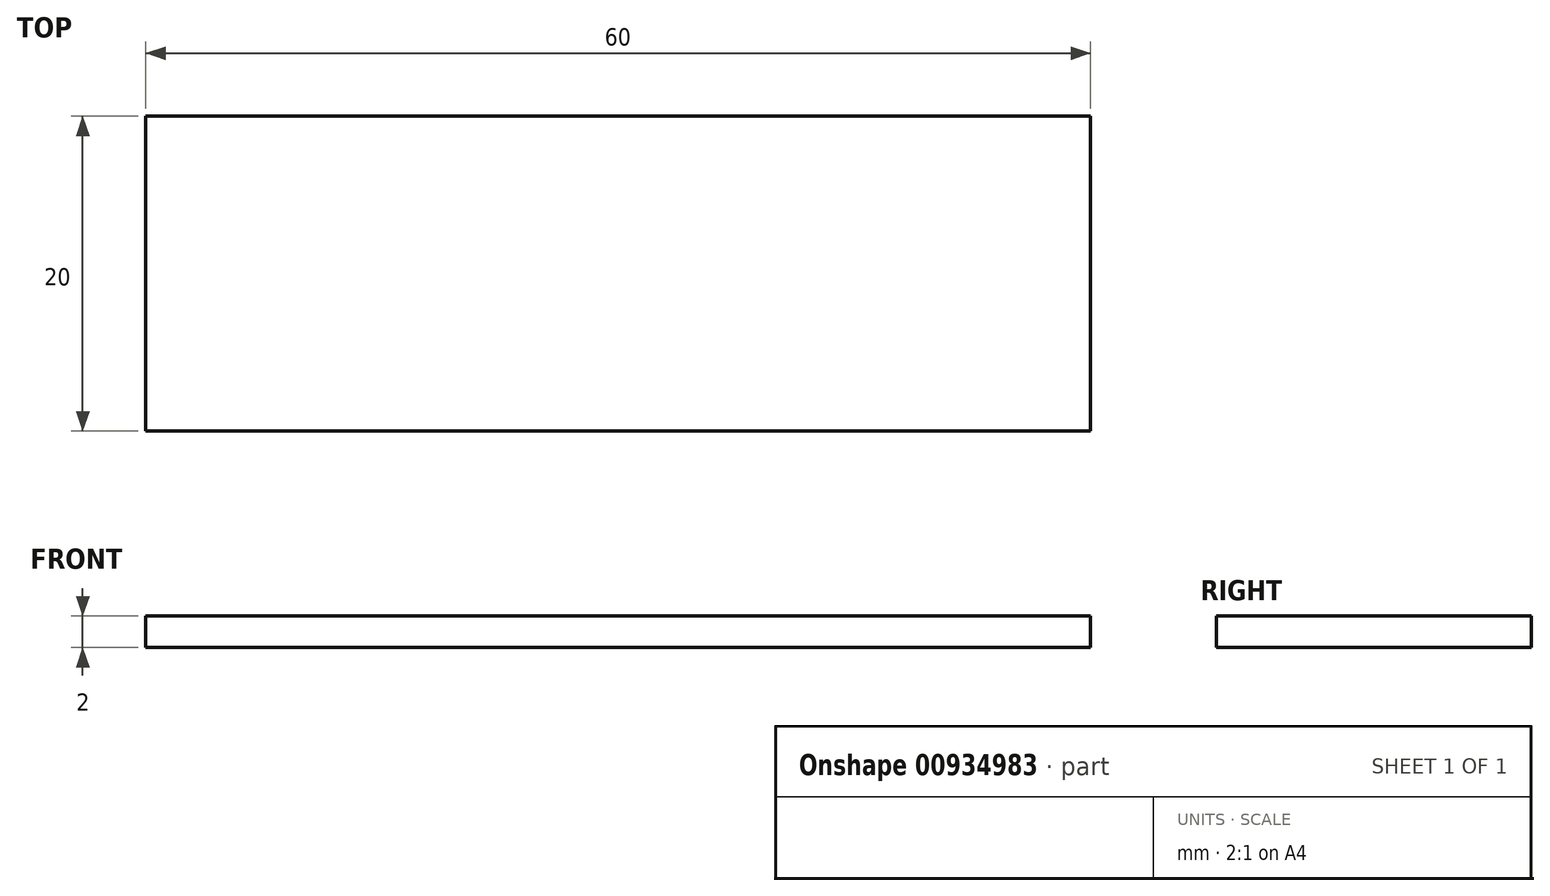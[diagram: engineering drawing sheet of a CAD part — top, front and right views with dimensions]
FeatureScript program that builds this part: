
annotation { "Feature Type Name" : "Feature", "Feature Type Description" : "" }
export const myFeature = defineFeature(function(context is Context, id is Id, definition is map)
    precondition{}
    {
        {
            var Q0;
            Q0=qCreatedBy(makeId("Top.planeOp"),FACE);
            var sketch = newSketch(context, id + "F0", { "sketchPlane" : qUnion([Q0])});
            skLineSegment(sketch, "E0.bottom", {"start": v(30, -10) * mm, "end": v(-30, -10) * mm});
            skLineSegment(sketch, "E0.top", {"start": v(30, 10) * mm, "end": v(-30, 10) * mm});
            skLineSegment(sketch, "E0.left", {"start": v(30, -10) * mm, "end": v(30, 10) * mm});
            skLineSegment(sketch, "E0.right", {"start": v(-30, -10) * mm, "end": v(-30, 10) * mm});
            skPoint(sketch, "E0.middle", {"position": v(0, 0) * mm});
            skLineSegment(sketch, "E1.bottom", {"start": v(-73.3, -58.13) * mm, "end": v(-88.16, -58.13) * mm});
            skLineSegment(sketch, "E1.top", {"start": v(-73.3, -35.95) * mm, "end": v(-88.16, -35.95) * mm});
            skLineSegment(sketch, "E1.left", {"start": v(-73.3, -58.13) * mm, "end": v(-73.3, -35.95) * mm});
            skLineSegment(sketch, "E1.right", {"start": v(-88.16, -58.13) * mm, "end": v(-88.16, -35.95) * mm});
            skPoint(sketch, "E1.middle", {"position": v(-80.73, -47.04) * mm});
            skSolve(sketch);
        }
        {
            var Q0;
            Q0=makeQuery(id+"F0.imprint","IMPRINT",FACE,{"disambiguationData":[TD([[makeQuery(id+"F0.imprint","IMPRINT",EDGE,{"derivedFrom":sQuery(id+"F0.wireOp",EDGE,"E0.bottom")}),-1.0]])]});
            extrude(context, id + "F1", {"entities" : qUnion([Q0]), "depth" : 2 * mm, "offsetDistance" : 25 * mm});
        }
    });
